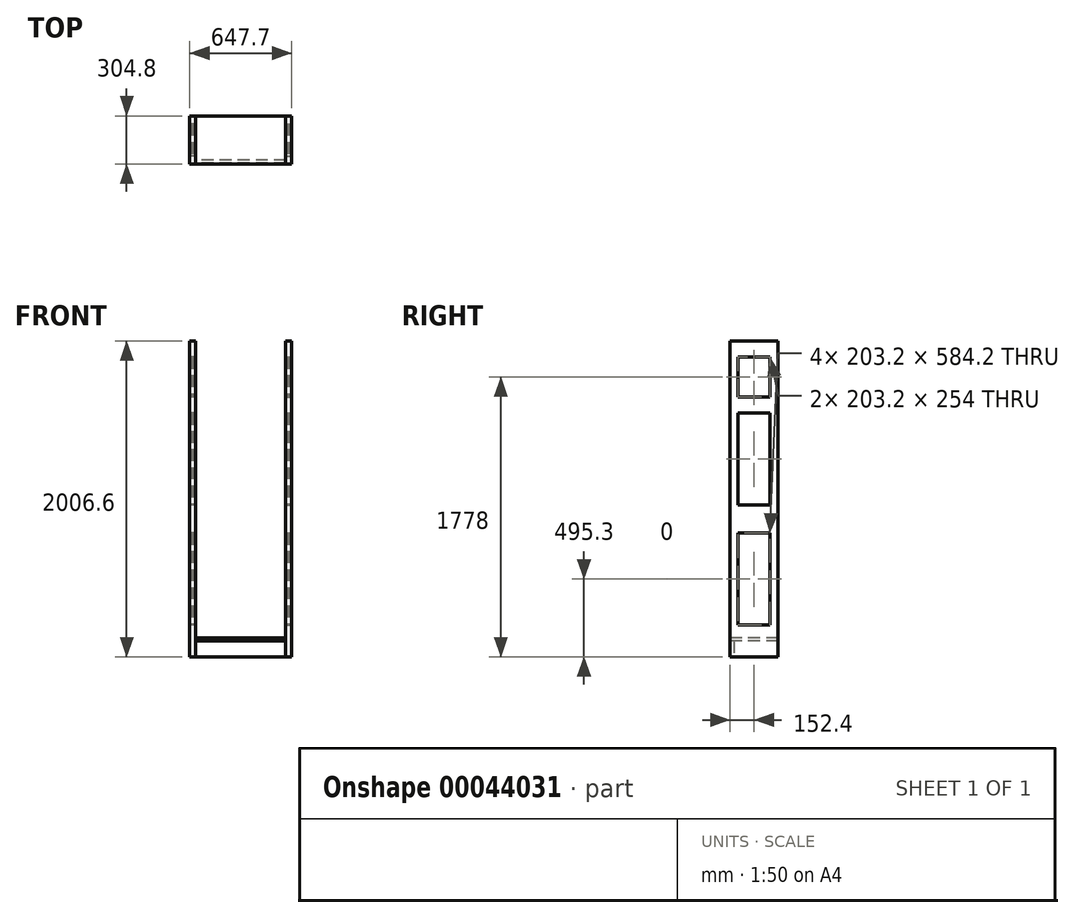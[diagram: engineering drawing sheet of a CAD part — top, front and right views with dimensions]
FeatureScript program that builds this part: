
annotation { "Feature Type Name" : "Feature", "Feature Type Description" : "" }
export const myFeature = defineFeature(function(context is Context, id is Id, definition is map)
    precondition{}
    {
        {
            var Q0;
            Q0=qCreatedBy(makeId("Right.planeOp"),FACE);
            var sketch = newSketch(context, id + "F0", { "sketchPlane" : qUnion([Q0])});
            skLineSegment(sketch, "E0.bottom", {"start": v(152.4, 1003.3) * mm, "end": v(-152.4, 1003.3) * mm});
            skLineSegment(sketch, "E0.top", {"start": v(152.4, -1003.3) * mm, "end": v(-152.4, -1003.3) * mm});
            skLineSegment(sketch, "E0.left", {"start": v(152.4, 1003.3) * mm, "end": v(152.4, -1003.3) * mm});
            skLineSegment(sketch, "E0.right", {"start": v(-152.4, 1003.3) * mm, "end": v(-152.4, -1003.3) * mm});
            skPoint(sketch, "E0.middle", {"position": v(0, 0) * mm});
            skLineSegment(sketch, "E1.0", {"start": v(101.6, -800.1) * mm, "end": v(-101.6, -800.1) * mm});
            skLineSegment(sketch, "E2.0", {"start": v(101.6, -215.9) * mm, "end": v(-101.6, -215.9) * mm});
            skLineSegment(sketch, "E3.0", {"start": v(101.6, -38.1) * mm, "end": v(-101.6, -38.1) * mm});
            skLineSegment(sketch, "E4.0", {"start": v(101.6, 546.1) * mm, "end": v(-101.6, 546.1) * mm});
            skLineSegment(sketch, "E5.0", {"start": v(101.6, 647.7) * mm, "end": v(-101.6, 647.7) * mm});
            skLineSegment(sketch, "E6.0", {"start": v(101.6, 901.7) * mm, "end": v(-101.6, 901.7) * mm});
            skLineSegment(sketch, "E7.0", {"start": v(-101.6, 901.7) * mm, "end": v(-101.6, 647.7) * mm});
            skLineSegment(sketch, "E8.0", {"start": v(101.6, 901.7) * mm, "end": v(101.6, 647.7) * mm});
            skLineSegment(sketch, "E9.trimOffspring", {"start": v(-101.6, -215.9) * mm, "end": v(-101.6, -800.1) * mm});
            skLineSegment(sketch, "E10.trimOffspring", {"start": v(101.6, -215.9) * mm, "end": v(101.6, -800.1) * mm});
            skLineSegment(sketch, "E11.trimOffspring", {"start": v(101.6, 546.1) * mm, "end": v(101.6, -38.1) * mm});
            skLineSegment(sketch, "E12.trimOffspring", {"start": v(-101.6, 546.1) * mm, "end": v(-101.6, -38.1) * mm});
            skSolve(sketch);
        }
        {
            var Q0;
            Q0 = qSketchRegion(id + "F0", true);
            extrude(context, id + "F1", {"entities" : qUnion([Q0]), "depth" : 38.1 * mm, "symmetric" : true});
        }
        {
            var Q0;
            Q0=makeQuery(id+"F0.imprint","IMPRINT",FACE,{"disambiguationData":[TD([[makeQuery(id+"F0.imprint","IMPRINT",EDGE,{"derivedFrom":sQuery(id+"F0.wireOp",EDGE,"E5.0")}),-1.0]])]});
            var Q1;
            Q1=makeQuery(id+"F0.imprint","IMPRINT",FACE,{"disambiguationData":[TD([[makeQuery(id+"F0.imprint","IMPRINT",EDGE,{"derivedFrom":sQuery(id+"F0.wireOp",EDGE,"E3.0")}),-1.0]])]});
            var Q2;
            Q2=makeQuery(id+"F0.imprint","IMPRINT",FACE,{"disambiguationData":[TD([[makeQuery(id+"F0.imprint","IMPRINT",EDGE,{"derivedFrom":sQuery(id+"F0.wireOp",EDGE,"E1.0")}),-1.0]])]});
            extrude(context, id + "F2", {"entities" : qUnion([Q0, Q1, Q2]), "depth" : 12.7 * mm, "symmetric" : true});
        }
        {
            var Q0;
            Q0=qCreatedBy(makeId("Right.planeOp"),FACE);
            cPlane(context, id + "F3", {"entities" : qUnion([Q0]), "cplaneType" : CPlaneType.OFFSET, "offset" : 304.8 * mm, "width" : 152.4 * mm, "height" : 152.4 * mm});
        }
        {
            var Q0;
            Q0=makeQuery(id+"F1.opExtrude","SWEPT_BODY",BODY,{"disambiguationData":[OSD([sQuery(id+"F0.wireOp",EDGE,"E0.bottom"),sQuery(id+"F0.wireOp",EDGE,"E0.top"),sQuery(id+"F0.wireOp",EDGE,"E0.left"),sQuery(id+"F0.wireOp",EDGE,"E0.right"),sQuery(id+"F0.wireOp",EDGE,"E1.0"),sQuery(id+"F0.wireOp",EDGE,"E2.0"),sQuery(id+"F0.wireOp",EDGE,"E3.0"),sQuery(id+"F0.wireOp",EDGE,"E4.0"),sQuery(id+"F0.wireOp",EDGE,"E5.0"),sQuery(id+"F0.wireOp",EDGE,"E6.0"),sQuery(id+"F0.wireOp",EDGE,"E7.0"),sQuery(id+"F0.wireOp",EDGE,"E8.0"),sQuery(id+"F0.wireOp",EDGE,"E9.trimOffspring"),sQuery(id+"F0.wireOp",EDGE,"E10.trimOffspring"),sQuery(id+"F0.wireOp",EDGE,"E11.trimOffspring"),sQuery(id+"F0.wireOp",EDGE,"E12.trimOffspring")])]});
            var Q1;
            Q1=makeQuery(id+"F2.opExtrude","SWEPT_BODY",BODY,{"disambiguationData":[OSD([sQuery(id+"F0.wireOp",EDGE,"E1.0"),sQuery(id+"F0.wireOp",EDGE,"E2.0"),sQuery(id+"F0.wireOp",EDGE,"E9.trimOffspring"),sQuery(id+"F0.wireOp",EDGE,"E10.trimOffspring")])]});
            var Q2;
            Q2=makeQuery(id+"F2.opExtrude","SWEPT_BODY",BODY,{"disambiguationData":[OSD([sQuery(id+"F0.wireOp",EDGE,"E3.0"),sQuery(id+"F0.wireOp",EDGE,"E4.0"),sQuery(id+"F0.wireOp",EDGE,"E11.trimOffspring"),sQuery(id+"F0.wireOp",EDGE,"E12.trimOffspring")])]});
            var Q3;
            Q3=makeQuery(id+"F2.opExtrude","SWEPT_BODY",BODY,{"disambiguationData":[OSD([sQuery(id+"F0.wireOp",EDGE,"E5.0"),sQuery(id+"F0.wireOp",EDGE,"E6.0"),sQuery(id+"F0.wireOp",EDGE,"E7.0"),sQuery(id+"F0.wireOp",EDGE,"E8.0")])]});
            var Q4;
            Q4=qCreatedBy(id+"F3.planeOp",FACE);
            mirror(context, id + "F4", {"entities" : qUnion([Q0, Q1, Q2, Q3]), "mirrorPlane" : qUnion([Q4])});
        }
        {
            var Q0;
            Q0=makeQuery(id+"F1.opExtrude","CAP_FACE",FACE,{"disambiguationData":[OSD([sQuery(id+"F0.wireOp",EDGE,"E0.bottom"),sQuery(id+"F0.wireOp",EDGE,"E0.top"),sQuery(id+"F0.wireOp",EDGE,"E0.left"),sQuery(id+"F0.wireOp",EDGE,"E0.right"),sQuery(id+"F0.wireOp",EDGE,"E1.0"),sQuery(id+"F0.wireOp",EDGE,"E2.0"),sQuery(id+"F0.wireOp",EDGE,"E3.0"),sQuery(id+"F0.wireOp",EDGE,"E4.0"),sQuery(id+"F0.wireOp",EDGE,"E5.0"),sQuery(id+"F0.wireOp",EDGE,"E6.0"),sQuery(id+"F0.wireOp",EDGE,"E7.0"),sQuery(id+"F0.wireOp",EDGE,"E8.0"),sQuery(id+"F0.wireOp",EDGE,"E9.trimOffspring"),sQuery(id+"F0.wireOp",EDGE,"E10.trimOffspring"),sQuery(id+"F0.wireOp",EDGE,"E11.trimOffspring"),sQuery(id+"F0.wireOp",EDGE,"E12.trimOffspring")])],"isStart":false});
            var sketch = newSketch(context, id + "F5", { "sketchPlane" : qUnion([Q0])});
            skLineSegment(sketch, "E13.0", {"start": v(152.4, -1003.3) * mm, "end": v(-152.4, -1003.3) * mm});
            skLineSegment(sketch, "E14.0", {"start": v(-152.4, 1003.3) * mm, "end": v(-152.4, -1003.3) * mm});
            skLineSegment(sketch, "E15.0", {"start": v(-146.05, 1003.3) * mm, "end": v(-146.05, -1003.3) * mm});
            skLineSegment(sketch, "E16.bottom", {"start": v(-146.05, -1003.3) * mm, "end": v(-127, -1003.3) * mm});
            skLineSegment(sketch, "E16.top", {"start": v(-146.05, -901.7) * mm, "end": v(-127, -901.7) * mm});
            skLineSegment(sketch, "E16.left", {"start": v(-146.05, -1003.3) * mm, "end": v(-146.05, -901.7) * mm});
            skLineSegment(sketch, "E16.right", {"start": v(-127, -1003.3) * mm, "end": v(-127, -901.7) * mm});
            skSolve(sketch);
        }
        {
            var Q0;
            Q0 = qSketchRegion(id + "F5", true);
            extrude(context, id + "F6", {"entities" : qUnion([Q0]), "endBound" : BoundingType.UP_TO_NEXT, "depth" : 25.4 * mm});
        }
        {
            var Q0;
            Q0=makeQuery(id+"F1.opExtrude","CAP_FACE",FACE,{"disambiguationData":[OSD([sQuery(id+"F0.wireOp",EDGE,"E0.bottom"),sQuery(id+"F0.wireOp",EDGE,"E0.top"),sQuery(id+"F0.wireOp",EDGE,"E0.left"),sQuery(id+"F0.wireOp",EDGE,"E0.right"),sQuery(id+"F0.wireOp",EDGE,"E1.0"),sQuery(id+"F0.wireOp",EDGE,"E2.0"),sQuery(id+"F0.wireOp",EDGE,"E3.0"),sQuery(id+"F0.wireOp",EDGE,"E4.0"),sQuery(id+"F0.wireOp",EDGE,"E5.0"),sQuery(id+"F0.wireOp",EDGE,"E6.0"),sQuery(id+"F0.wireOp",EDGE,"E7.0"),sQuery(id+"F0.wireOp",EDGE,"E8.0"),sQuery(id+"F0.wireOp",EDGE,"E9.trimOffspring"),sQuery(id+"F0.wireOp",EDGE,"E10.trimOffspring"),sQuery(id+"F0.wireOp",EDGE,"E11.trimOffspring"),sQuery(id+"F0.wireOp",EDGE,"E12.trimOffspring")])],"isStart":false});
            var sketch = newSketch(context, id + "F7", { "sketchPlane" : qUnion([Q0])});
            skLineSegment(sketch, "E17.0", {"start": v(-146.05, -901.7) * mm, "end": v(-127, -901.7) * mm});
            skLineSegment(sketch, "E18.0", {"start": v(-152.4, 1003.3) * mm, "end": v(-152.4, -1003.3) * mm});
            skLineSegment(sketch, "E19.0", {"start": v(152.4, 1003.3) * mm, "end": v(152.4, -1003.3) * mm});
            skLineSegment(sketch, "E20.bottom", {"start": v(-152.4, -882.65) * mm, "end": v(152.4, -882.65) * mm});
            skLineSegment(sketch, "E20.top", {"start": v(-152.4, -901.7) * mm, "end": v(152.4, -901.7) * mm});
            skLineSegment(sketch, "E20.left", {"start": v(-152.4, -882.65) * mm, "end": v(-152.4, -901.7) * mm});
            skLineSegment(sketch, "E20.right", {"start": v(152.4, -882.65) * mm, "end": v(152.4, -901.7) * mm});
            skSolve(sketch);
        }
        {
            var Q0;
            Q0 = qSketchRegion(id + "F7", true);
            extrude(context, id + "F8", {"entities" : qUnion([Q0]), "endBound" : BoundingType.UP_TO_NEXT, "depth" : 25.4 * mm});
        }
    });
